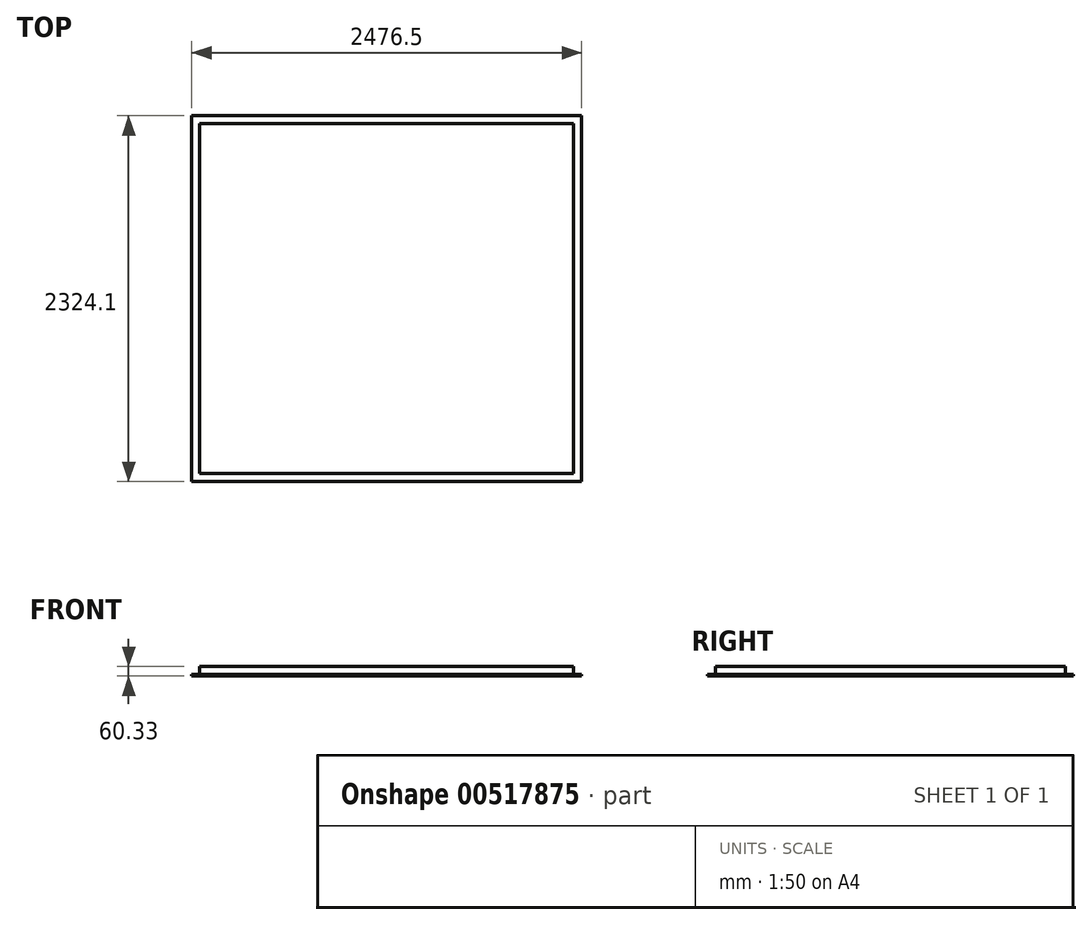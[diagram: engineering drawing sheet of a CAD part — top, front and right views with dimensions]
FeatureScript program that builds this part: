
annotation { "Feature Type Name" : "Feature", "Feature Type Description" : "" }
export const myFeature = defineFeature(function(context is Context, id is Id, definition is map)
    precondition{}
    {
        {
            var Q0;
            Q0=qCreatedBy(makeId("Top.planeOp"),FACE);
            var sketch = newSketch(context, id + "F0", { "sketchPlane" : qUnion([Q0])});
            skLineSegment(sketch, "E0.bottom", {"start": v(0, 0) * mm, "end": v(2374.9, 0) * mm});
            skLineSegment(sketch, "E0.top", {"start": v(0, 2222.5) * mm, "end": v(2374.9, 2222.5) * mm});
            skLineSegment(sketch, "E0.left", {"start": v(0, 0) * mm, "end": v(0, 2222.5) * mm});
            skLineSegment(sketch, "E0.right", {"start": v(2374.9, 0) * mm, "end": v(2374.9, 2222.5) * mm});
            skSolve(sketch);
        }
        {
            var Q0;
            Q0=makeQuery(id+"F0.imprint","IMPRINT",FACE,{"disambiguationData":[TD([[makeQuery(id+"F0.imprint","IMPRINT",EDGE,{"derivedFrom":sQuery(id+"F0.wireOp",EDGE,"E0.bottom")}),1.0]])]});
            extrude(context, id + "F1", {"entities" : qUnion([Q0]), "depth" : 50.8 * mm, "offsetDistance" : 25.4 * mm});
        }
        {
            var Q0;
            Q0=makeQuery(id+"F1.opExtrude","CAP_FACE",FACE,{"disambiguationData":[OSD([sQuery(id+"F0.wireOp",EDGE,"E0.bottom"),sQuery(id+"F0.wireOp",EDGE,"E0.top"),sQuery(id+"F0.wireOp",EDGE,"E0.left"),sQuery(id+"F0.wireOp",EDGE,"E0.right")])],"isStart":true});
            var sketch = newSketch(context, id + "F2", { "sketchPlane" : qUnion([Q0])});
            skLineSegment(sketch, "E1.bottom", {"start": v(0, 0) * mm, "end": v(2374.9, 0) * mm, "construction": true});
            skLineSegment(sketch, "E1.top", {"start": v(0, -2222.5) * mm, "end": v(2374.9, -2222.5) * mm, "construction": true});
            skLineSegment(sketch, "E1.left", {"start": v(0, 0) * mm, "end": v(0, -2222.5) * mm, "construction": true});
            skLineSegment(sketch, "E1.right", {"start": v(2374.9, 0) * mm, "end": v(2374.9, -2222.5) * mm, "construction": true});
            skLineSegment(sketch, "E2.0", {"start": v(-50.8, 50.8) * mm, "end": v(2425.7, 50.8) * mm});
            skLineSegment(sketch, "E2.1", {"start": v(-50.8, 50.8) * mm, "end": v(-50.8, -2273.3) * mm});
            skLineSegment(sketch, "E2.2", {"start": v(-50.8, -2273.3) * mm, "end": v(2425.7, -2273.3) * mm});
            skLineSegment(sketch, "E2.3", {"start": v(2425.7, 50.8) * mm, "end": v(2425.7, -2273.3) * mm});
            skSolve(sketch);
        }
        {
            var Q0;
            Q0 = qSketchRegion(id + "F2", true);
            extrude(context, id + "F3", {"entities" : qUnion([Q0]), "depth" : 9.52 * mm, "offsetDistance" : 25.4 * mm});
        }
    });
